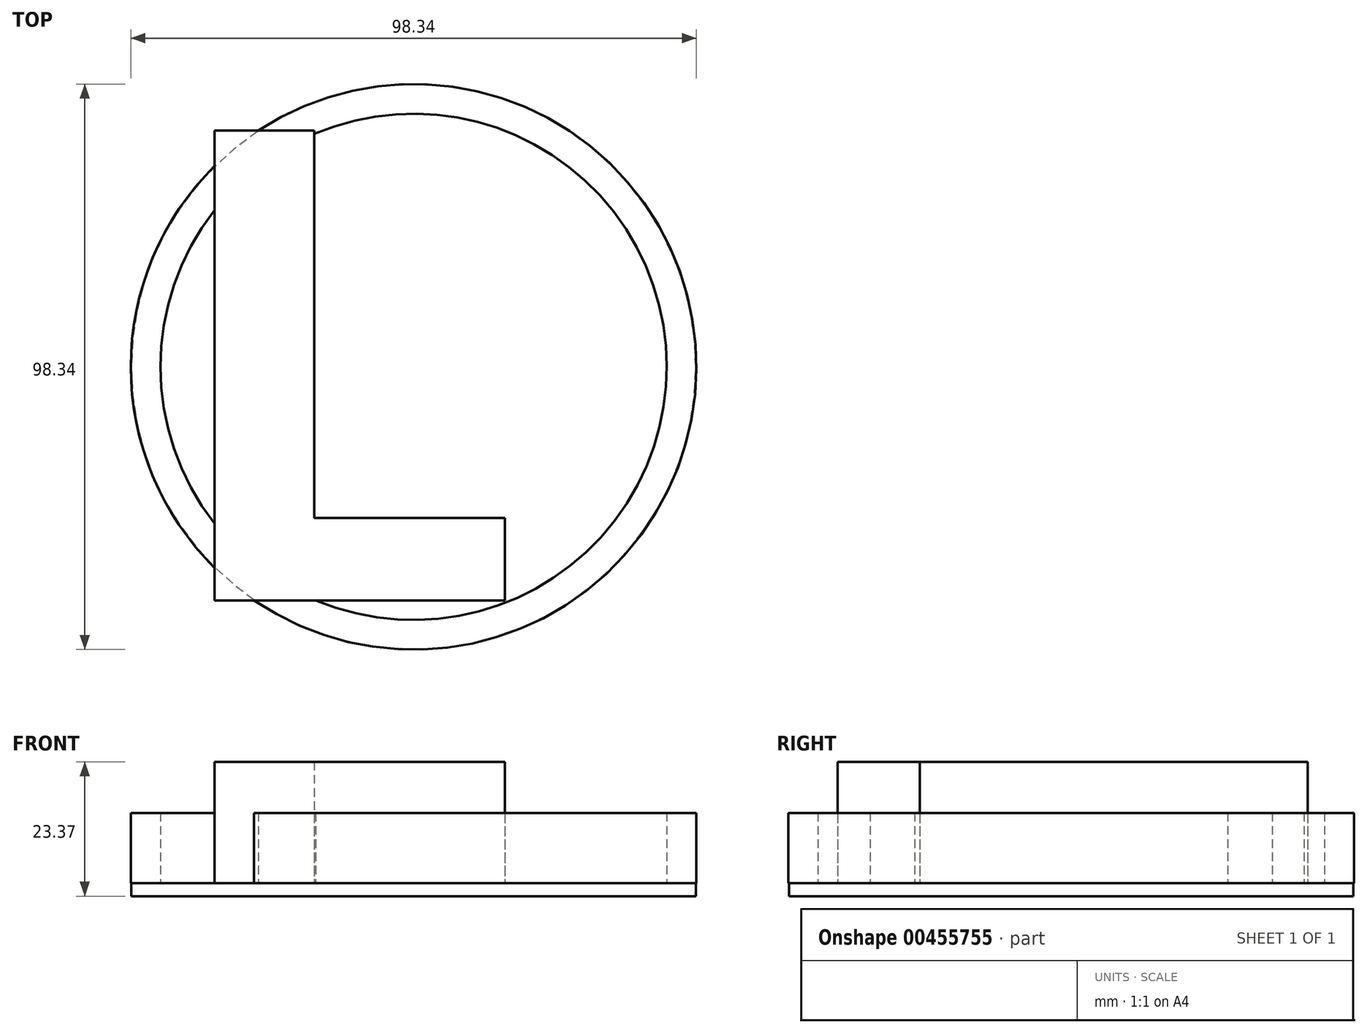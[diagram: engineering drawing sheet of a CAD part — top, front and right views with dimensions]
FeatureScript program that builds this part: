
annotation { "Feature Type Name" : "Feature", "Feature Type Description" : "" }
export const myFeature = defineFeature(function(context is Context, id is Id, definition is map)
    precondition{}
    {
        {
            var Q0;
            Q0=qCreatedBy(makeId("Top.planeOp"),FACE);
            var sketch = newSketch(context, id + "F0", { "sketchPlane" : qUnion([Q0])});
            skCircle(sketch, "E0", {"center": v(0, 0) * mm, "radius": 49.17 * mm});
            skCircle(sketch, "E1", {"center": v(0, 0) * mm, "radius": 44.02 * mm});
            skSolve(sketch);
        }
        {
            var Q0;
            Q0=makeQuery(id+"F0.imprint","IMPRINT",FACE,{"disambiguationData":[TD([[makeQuery(id+"F0.imprint","IMPRINT",EDGE,{"derivedFrom":sQuery(id+"F0.wireOp",EDGE,"E1")}),1.0]])]});
            var sketch = newSketch(context, id + "F1", { "sketchPlane" : qUnion([Q0])});
            skText(sketch, "E2", { "text": "L", "fontName": "OpenSans-Bold.ttf"});
            const initialGuessF1  = {"E2": [-0.04486, -0.0406, 1, 0, 0.08239]};
            skSetInitialGuess(sketch, initialGuessF1);
            skSolve(sketch);
        }
        {
            var Q0;
            Q0=makeQuery(id+"F0.imprint","IMPRINT",FACE,{"disambiguationData":[TD([[makeQuery(id+"F0.imprint","IMPRINT",EDGE,{"derivedFrom":sQuery(id+"F0.wireOp",EDGE,"E1")}),1.0]])]});
            var sketch = newSketch(context, id + "F2", { "sketchPlane" : qUnion([Q0])});
            skFitSpline(sketch, "E3", {"points": [v(-16.97, -25.17) * mm, v(17.19, 0) * mm, v(43.18, -6.05) * mm, v(43.18, -6.42) * mm], "startDerivative": vector(56.7, 67.58) * mm, "endDerivative": vector(-3.59, -6.28) * mm});
            skFitSpline(sketch, "E4", {"points": [v(-2.5, -25.72) * mm, v(12.55, -20.9) * mm, v(24.61, -24.8) * mm, v(31.3, -20.34) * mm, v(32.97, -14.03) * mm, v(43.24, -11.8) * mm], "startDerivative": vector(62.43, 33.36) * mm, "endDerivative": vector(65.04, 2.41) * mm});
            skFitSpline(sketch, "E5", {"points": [v(-34.98, 9.73) * mm, v(-43.33, 8.62) * mm, v(-42.22, 12.52) * mm], "startDerivative": vector(-19.13, -5.25) * mm, "endDerivative": vector(6.17, 11.85) * mm});
            skFitSpline(sketch, "E6", {"points": [v(-41.85, -12.92) * mm, v(-34.6, -13.1) * mm], "startDerivative": vector(7.24, -0.19) * mm, "endDerivative": vector(7.24, -0.19) * mm});
            skFitSpline(sketch, "E7", {"points": [v(27.03, 34.05) * mm, v(18.12, 32.38) * mm, v(16.45, 29.41) * mm], "startDerivative": vector(-17.47, -1.1) * mm, "endDerivative": vector(-2.5, -8.79) * mm});
            skFitSpline(sketch, "E8", {"points": [v(16.45, 29.41) * mm, v(0, 19.39) * mm, v(-16.97, 10.85) * mm, v(-16.97, 29.41) * mm], "startDerivative": vector(-45, -25.45) * mm, "endDerivative": vector(13.6, 77.67) * mm});
            skSolve(sketch);
        }
        {
            var Q0;
            Q0 = qSketchRegion(id + "F0", true);
            extrude(context, id + "F3", {"entities" : qUnion([Q0]), "depth" : 12.2 * mm});
        }
        {
            var Q0;
            Q0 = qSketchRegion(id + "F1", true);
            extrude(context, id + "F4", {"entities" : qUnion([Q0]), "operationType" : NewBodyOperationType.ADD, "depth" : 21.08 * mm});
        }
        {
            var Q0;
            Q0 = qSketchRegion(id + "F2", true);
            var Q1;
            Q1=sQuery(id+"F2.wireOp",EDGE,"E8");
            var Q2;
            Q2=sQuery(id+"F2.wireOp",EDGE,"E7");
            var Q3;
            Q3=sQuery(id+"F2.wireOp",EDGE,"E3");
            var Q4;
            Q4=sQuery(id+"F2.wireOp",EDGE,"E6");
            var Q5;
            Q5=sQuery(id+"F2.wireOp",EDGE,"E5");
            var Q6;
            Q6=sQuery(id+"F2.wireOp",EDGE,"E4");
            extrude(context, id + "F5", {"entities" : qUnion([Q0]), "bodyType" : ToolBodyType.SURFACE, "surfaceEntities" : qUnion([Q1, Q2, Q3, Q4, Q5, Q6]), "depth" : 14.22 * mm});
        }
        {
            var Q0;
            Q0=qCreatedBy(makeId("Top.planeOp"),FACE);
            var sketch = newSketch(context, id + "F6", { "sketchPlane" : qUnion([Q0])});
            skCircle(sketch, "E9", {"center": v(0, 0) * mm, "radius": 49.07 * mm});
            skSolve(sketch);
        }
        {
            var Q0;
            Q0 = qSketchRegion(id + "F6", true);
            extrude(context, id + "F7", {"entities" : qUnion([Q0]), "operationType" : NewBodyOperationType.ADD, "oppositeDirection" : true, "depth" : 2.3 * mm});
        }
    });
